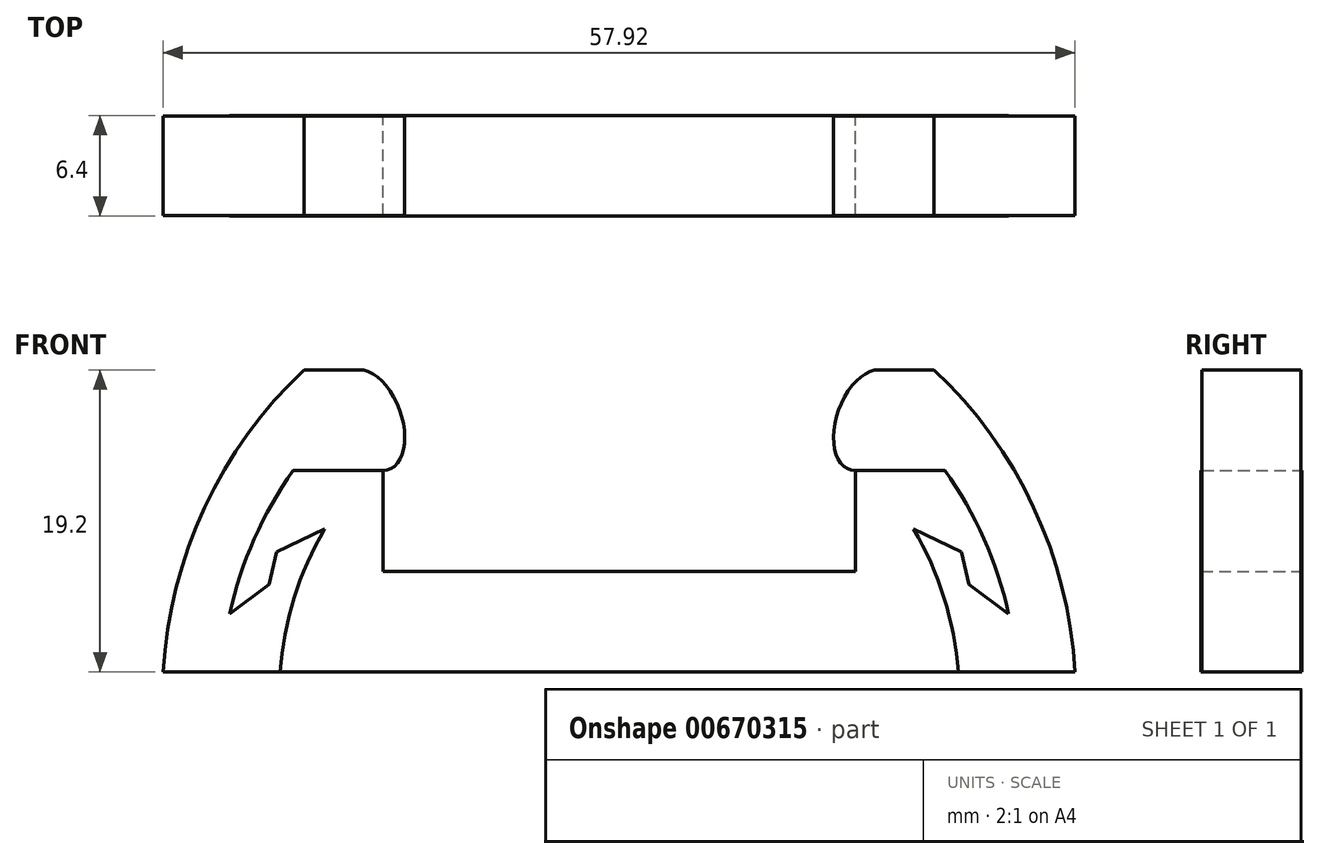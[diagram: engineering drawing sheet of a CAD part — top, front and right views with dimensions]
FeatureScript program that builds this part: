
annotation { "Feature Type Name" : "Feature", "Feature Type Description" : "" }
export const myFeature = defineFeature(function(context is Context, id is Id, definition is map)
    precondition{}
    {
        {
            assignVariable(context, id + "F0", {"name" : "thickness", "anyValue" : 6.4});
        }
        {
            var Q0;
            Q0=qCreatedBy(makeId("Front.planeOp"),FACE);
            var sketch = newSketch(context, id + "F1", { "sketchPlane" : qUnion([Q0])});
            skLineSegment(sketch, "E0", {"start": v(-16.5, 19.2) * mm, "end": v(-20, 19.2) * mm});
            skLineSegment(sketch, "E1", {"start": v(16.5, 19.2) * mm, "end": v(20, 19.2) * mm});
            skArc(sketch, "E2", {"start": v(-29, -1.6) * mm, "mid": v(-28.99, -0.8) * mm, "end": v(-28.96, 0) * mm, "construction": true});
            skArc(sketch, "E3", {"start": v(28.96, 0) * mm, "mid": v(26.33, 10.46) * mm, "end": v(20, 19.2) * mm});
            skPoint(sketch, "E4", {"position": v(-16.5, 19.2) * mm});
            skPoint(sketch, "E5", {"position": v(-15, 12.8) * mm});
            skLineSegment(sketch, "E6", {"start": v(-15, 12.8) * mm, "end": v(-15, 6.4) * mm});
            skPoint(sketch, "E7", {"position": v(16.5, 19.2) * mm});
            skPoint(sketch, "E8", {"position": v(15, 12.8) * mm});
            skLineSegment(sketch, "E9", {"start": v(15, 12.8) * mm, "end": v(15, 6.4) * mm});
            skPoint(sketch, "E10", {"position": v(-20.7, 12.8) * mm});
            skLineSegment(sketch, "E11", {"start": v(-20.7, 12.8) * mm, "end": v(-15, 12.8) * mm});
            skArc(sketch, "E12", {"start": v(-20.7, 12.8) * mm, "mid": v(-23.17, 8.45) * mm, "end": v(-24.73, 3.7) * mm});
            skPoint(sketch, "E13", {"position": v(24.73, 3.7) * mm});
            skPoint(sketch, "E14", {"position": v(20.7, 12.8) * mm});
            skLineSegment(sketch, "E15", {"start": v(20.7, 12.8) * mm, "end": v(15, 12.8) * mm});
            skArc(sketch, "E16", {"start": v(24.73, 3.7) * mm, "mid": v(23.17, 8.45) * mm, "end": v(20.7, 12.8) * mm});
            skEllipticalArc(sketch, "E17", {});
            skPoint(sketch, "E18", {"position": v(-13.75, 16) * mm});
            skEllipticalArc(sketch, "E19", {});
            skPoint(sketch, "E20", {"position": v(13.75, 16) * mm});
            skArc(sketch, "E21", {"start": v(-21.54, 0) * mm, "mid": v(-20.64, 4.7) * mm, "end": v(-18.7, 9.09) * mm});
            skLineSegment(sketch, "E22", {"start": v(-24.73, 3.7) * mm, "end": v(-22.22, 5.56) * mm});
            skLineSegment(sketch, "E23", {"start": v(-22.22, 5.56) * mm, "end": v(-21.75, 7.63) * mm});
            skLineSegment(sketch, "E24", {"start": v(-21.75, 7.63) * mm, "end": v(-18.7, 9.09) * mm});
            skArc(sketch, "E25", {"start": v(21.54, 0) * mm, "mid": v(20.64, 4.7) * mm, "end": v(18.7, 9.09) * mm});
            skLineSegment(sketch, "E26", {"start": v(18.7, 9.09) * mm, "end": v(21.75, 7.63) * mm});
            skLineSegment(sketch, "E27", {"start": v(21.75, 7.63) * mm, "end": v(22.22, 5.56) * mm});
            skLineSegment(sketch, "E28", {"start": v(22.22, 5.56) * mm, "end": v(24.73, 3.7) * mm});
            skLineSegment(sketch, "E29", {"start": v(-15, 6.4) * mm, "end": v(15, 6.4) * mm});
            skPoint(sketch, "E30", {"position": v(-28.96, 0) * mm});
            skLineSegment(sketch, "E31", {"start": v(-28.96, 0) * mm, "end": v(28.96, 0) * mm});
            skArc(sketch, "E32", {"start": v(-28.96, 0) * mm, "mid": v(-26.33, 10.46) * mm, "end": v(-20, 19.2) * mm});
            const initialGuessF1  = {"E17": [-0.01575, 0.016, 0.3437629429827801, -0.9390564621107168, 0.003334452651494432, 0.0019193554891630109, 6.075507126811803, 2.9339144873296554], "E19": [0.01575, 0.016, 0.34376295050095396, 0.9390564593585309, 0.0033344526572398835, 0.0019193554993947016, 0.207678186099478, 3.349270839689266]};
            skSetInitialGuess(sketch, initialGuessF1);
            skSolve(sketch);
        }
        {
            var Q0;
            Q0=makeQuery(id+"F1.imprint","IMPRINT",FACE,{"disambiguationData":[TD([[makeQuery(id+"F1.imprint","IMPRINT",EDGE,{"derivedFrom":sQuery(id+"F1.wireOp",EDGE,"E6")}),-1.0]])]});
            extrude(context, id + "F2", {"entities" : qUnion([Q0]), "endBound" : BoundingType.SYMMETRIC, "depth" : (getVariable(context, 'thickness')) * mm, "offsetDistance" : 25 * mm});
        }
        {
            var Q0;
            Q0=makeQuery(id+"F1.imprint","IMPRINT",FACE,{"disambiguationData":[TD([[makeQuery(id+"F1.imprint","IMPRINT",EDGE,{"derivedFrom":sQuery(id+"F1.wireOp",EDGE,"E0")}),1.0]])]});
            var Q1;
            Q1=makeQuery(id+"F1.imprint","IMPRINT",FACE,{"disambiguationData":[TD([[makeQuery(id+"F1.imprint","IMPRINT",EDGE,{"derivedFrom":sQuery(id+"F1.wireOp",EDGE,"E1")}),-1.0]])]});
            extrude(context, id + "F3", {"entities" : qUnion([Q0, Q1]), "operationType" : NewBodyOperationType.ADD, "endBound" : BoundingType.SYMMETRIC, "depth" : (getVariable(context, 'thickness') - 0.1) * mm, "offsetDistance" : 25 * mm});
        }
    });
